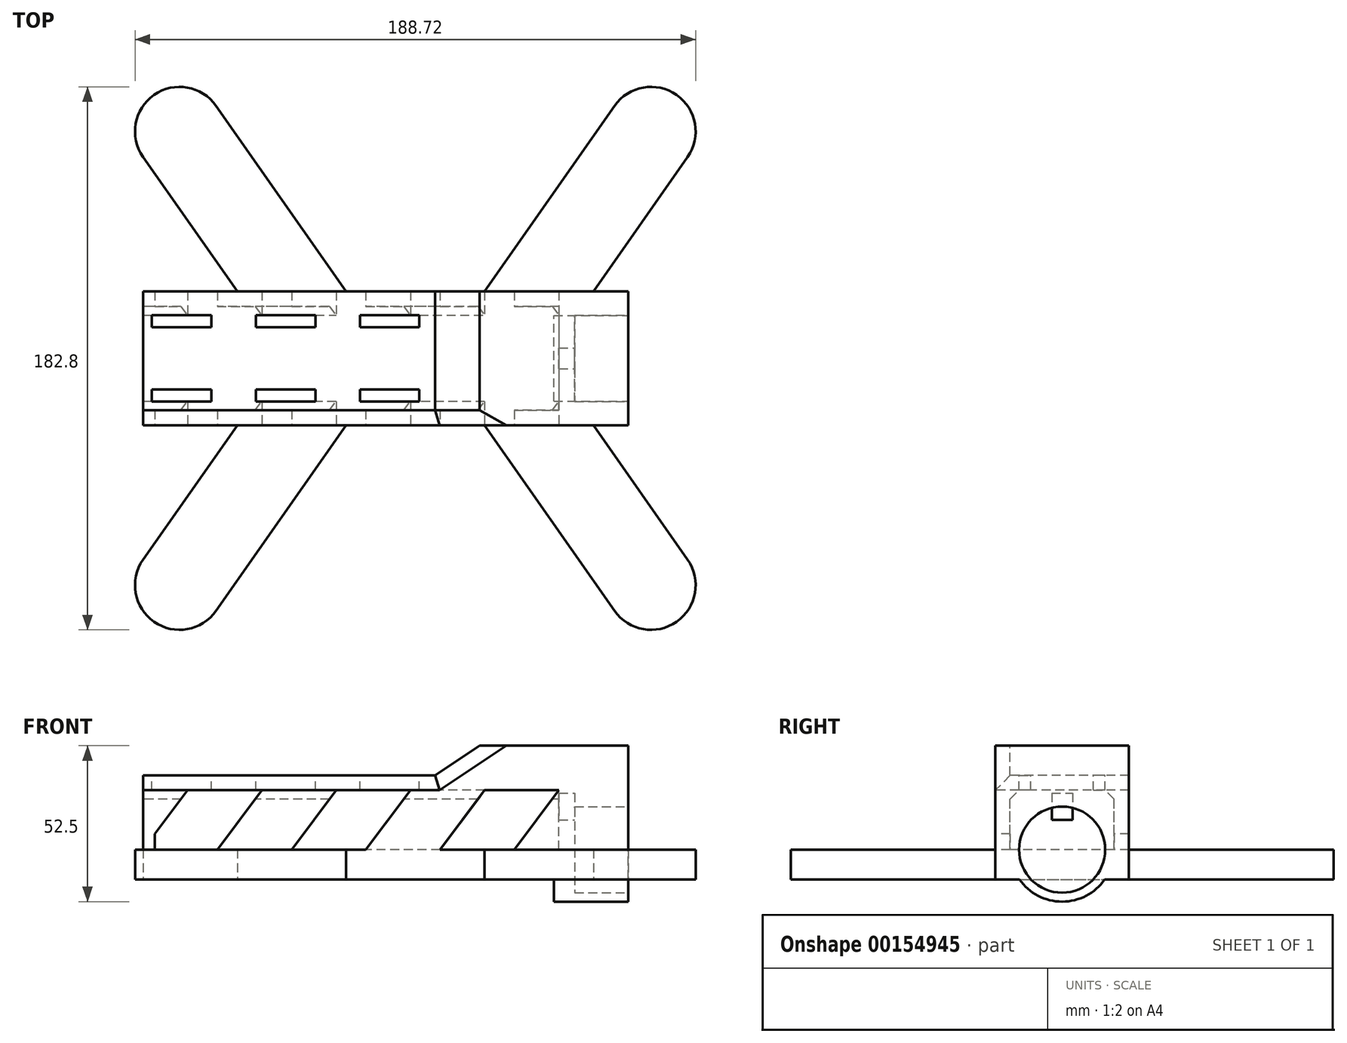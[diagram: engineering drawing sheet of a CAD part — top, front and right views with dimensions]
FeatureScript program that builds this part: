
annotation { "Feature Type Name" : "Feature", "Feature Type Description" : "" }
export const myFeature = defineFeature(function(context is Context, id is Id, definition is map)
    precondition{}
    {
        {
            var Q0;
            Q0=qCreatedBy(makeId("Top.planeOp"),FACE);
            var sketch = newSketch(context, id + "F0", { "sketchPlane" : qUnion([Q0])});
            skLineSegment(sketch, "E0.bottom", {"start": v(-91.65, 85) * mm, "end": v(91.65, 85) * mm, "construction": true});
            skLineSegment(sketch, "E0.top", {"start": v(-91.65, -85) * mm, "end": v(91.65, -85) * mm, "construction": true});
            skLineSegment(sketch, "E0.left", {"start": v(-91.65, 85) * mm, "end": v(-91.65, -85) * mm, "construction": true});
            skLineSegment(sketch, "E0.right", {"start": v(91.65, 85) * mm, "end": v(91.65, -85) * mm, "construction": true});
            skPoint(sketch, "E0.middle", {"position": v(0, 0) * mm});
            skLineSegment(sketch, "E1.bottom", {"start": v(-91.65, -22.5) * mm, "end": v(91.65, -22.5) * mm});
            skLineSegment(sketch, "E1.top", {"start": v(-91.65, 22.5) * mm, "end": v(91.65, 22.5) * mm});
            skLineSegment(sketch, "E1.left", {"start": v(-91.65, -22.5) * mm, "end": v(-91.65, 22.5) * mm});
            skLineSegment(sketch, "E1.right", {"start": v(91.65, -22.5) * mm, "end": v(91.65, 22.5) * mm});
            skLineSegment(sketch, "E2", {"start": v(-59.94, -22.5) * mm, "end": v(-91.65, -67.8) * mm});
            skLineSegment(sketch, "E3", {"start": v(-91.65, -67.8) * mm, "end": v(-67.08, -85) * mm});
            skLineSegment(sketch, "E4", {"start": v(-67.08, -85) * mm, "end": v(-23.31, -22.5) * mm});
            skCircle(sketch, "E5", {"center": v(-79.36, -76.4) * mm, "radius": 15 * mm});
            skCircle(sketch, "E6.MirrorC", {"center": v(79.36, -76.4) * mm, "radius": 15 * mm});
            skLineSegment(sketch, "E7.MirrorCS", {"start": v(59.94, -22.5) * mm, "end": v(91.65, -67.8) * mm});
            skLineSegment(sketch, "E8.MirrorCS", {"start": v(67.08, -85) * mm, "end": v(23.31, -22.5) * mm});
            skLineSegment(sketch, "E9.MirrorCS", {"start": v(59.94, 22.5) * mm, "end": v(91.65, 67.8) * mm});
            skCircle(sketch, "E10.MirrorC", {"center": v(79.36, 76.4) * mm, "radius": 15 * mm});
            skLineSegment(sketch, "E11.MirrorCS", {"start": v(67.08, 85) * mm, "end": v(23.31, 22.5) * mm});
            skCircle(sketch, "E12.MirrorC", {"center": v(-79.36, 76.4) * mm, "radius": 15 * mm});
            skLineSegment(sketch, "E13.MirrorCS", {"start": v(-67.08, 85) * mm, "end": v(-23.31, 22.5) * mm});
            skLineSegment(sketch, "E14.MirrorCS", {"start": v(-59.94, 22.5) * mm, "end": v(-91.65, 67.8) * mm});
            skSolve(sketch);
        }
        {
            var Q0;
            Q0 = qSketchRegion(id + "F0", true);
            extrude(context, id + "F1", {"entities" : qUnion([Q0]), "depth" : 45 * mm});
        }
        {
            var Q0;
            Q0=makeQuery(id+"F1.opExtrude","CAP_FACE",FACE,{"disambiguationData":[OSD([sQuery(id+"F0.wireOp",EDGE,"E1.bottom"),sQuery(id+"F0.wireOp",EDGE,"E1.top"),sQuery(id+"F0.wireOp",EDGE,"E1.left"),sQuery(id+"F0.wireOp",EDGE,"E1.right"),sQuery(id+"F0.wireOp",EDGE,"E2"),sQuery(id+"F0.wireOp",EDGE,"E4"),sQuery(id+"F0.wireOp",EDGE,"E5"),sQuery(id+"F0.wireOp",EDGE,"E6.MirrorC"),sQuery(id+"F0.wireOp",EDGE,"E7.MirrorCS"),sQuery(id+"F0.wireOp",EDGE,"E8.MirrorCS"),sQuery(id+"F0.wireOp",EDGE,"E9.MirrorCS"),sQuery(id+"F0.wireOp",EDGE,"E10.MirrorC"),sQuery(id+"F0.wireOp",EDGE,"E11.MirrorCS"),sQuery(id+"F0.wireOp",EDGE,"E12.MirrorC"),sQuery(id+"F0.wireOp",EDGE,"E13.MirrorCS"),sQuery(id+"F0.wireOp",EDGE,"E14.MirrorCS")])],"isStart":false});
            var sketch = newSketch(context, id + "F2", { "sketchPlane" : qUnion([Q0])});
            skLineSegment(sketch, "E15.bottom", {"start": v(-91.65, 22.5) * mm, "end": v(91.65, 22.5) * mm});
            skLineSegment(sketch, "E15.top", {"start": v(-91.65, -22.5) * mm, "end": v(91.65, -22.5) * mm});
            skLineSegment(sketch, "E15.left", {"start": v(-91.65, 22.5) * mm, "end": v(-91.65, -22.5) * mm});
            skLineSegment(sketch, "E15.right", {"start": v(91.65, 22.5) * mm, "end": v(91.65, -22.5) * mm});
            skPoint(sketch, "E15.middle", {"position": v(0, 0) * mm});
            skLineSegment(sketch, "E16.bottom", {"start": v(-108.28, -99.99) * mm, "end": v(108.28, -99.99) * mm});
            skLineSegment(sketch, "E16.top", {"start": v(-108.28, 99.99) * mm, "end": v(108.28, 99.99) * mm});
            skLineSegment(sketch, "E16.left", {"start": v(-108.28, -99.99) * mm, "end": v(-108.28, 99.99) * mm});
            skLineSegment(sketch, "E16.right", {"start": v(108.28, -99.99) * mm, "end": v(108.28, 99.99) * mm});
            skSolve(sketch);
        }
        {
            var Q0;
            Q0 = qSketchRegion(id + "F2", true);
            extrude(context, id + "F3", {"entities" : qUnion([Q0]), "operationType" : NewBodyOperationType.REMOVE, "oppositeDirection" : true, "depth" : 35 * mm});
        }
        {
            var Q0;
            Q0=makeQuery(id+"F1.opExtrude","SWEPT_FACE",FACE,{"disambiguationData":[OSD([sQuery(id+"F0.wireOp",EDGE,"E1.right")])]});
            var sketch = newSketch(context, id + "F4", { "sketchPlane" : qUnion([Q0])});
            skLineSegment(sketch, "E17.bottom", {"start": v(-22.5, 0) * mm, "end": v(22.5, 0) * mm});
            skLineSegment(sketch, "E17.top", {"start": v(-22.5, 45) * mm, "end": v(22.5, 45) * mm});
            skLineSegment(sketch, "E17.left", {"start": v(-22.5, 0) * mm, "end": v(-22.5, 45) * mm});
            skLineSegment(sketch, "E17.right", {"start": v(22.5, 0) * mm, "end": v(22.5, 45) * mm});
            skSolve(sketch);
        }
        {
            var Q0;
            Q0 = qSketchRegion(id + "F4", true);
            extrude(context, id + "F5", {"entities" : qUnion([Q0]), "operationType" : NewBodyOperationType.REMOVE, "oppositeDirection" : true, "depth" : 20 * mm});
        }
        {
            var Q0;
            Q0=makeQuery(id+"F5.boolean.opBoolean","COPY",FACE,{"derivedFrom":makeQuery(id+"F5.opExtrude","CAP_FACE",FACE,{"disambiguationData":[OSD([sQuery(id+"F4.wireOp",EDGE,"E17.bottom"),sQuery(id+"F4.wireOp",EDGE,"E17.top"),sQuery(id+"F4.wireOp",EDGE,"E17.left"),sQuery(id+"F4.wireOp",EDGE,"E17.right")])],"isStart":false})});
            var sketch = newSketch(context, id + "F6", { "sketchPlane" : qUnion([Q0])});
            skCircle(sketch, "E18", {"center": v(0, 10) * mm, "radius": 17.5 * mm});
            skSolve(sketch);
        }
        {
            var Q0;
            Q0 = qSketchRegion(id + "F6", true);
            extrude(context, id + "F7", {"entities" : qUnion([Q0]), "operationType" : NewBodyOperationType.ADD, "oppositeDirection" : true, "depth" : 25 * mm});
        }
        {
            var Q0;
            Q0=makeQuery(id+"F5.boolean.opBoolean","COPY",FACE,{"derivedFrom":makeQuery(id+"F5.opExtrude","CAP_FACE",FACE,{"disambiguationData":[OSD([sQuery(id+"F4.wireOp",EDGE,"E17.bottom"),sQuery(id+"F4.wireOp",EDGE,"E17.top"),sQuery(id+"F4.wireOp",EDGE,"E17.left"),sQuery(id+"F4.wireOp",EDGE,"E17.right")])],"isStart":false})});
            var sketch = newSketch(context, id + "F8", { "sketchPlane" : qUnion([Q0])});
            skCircle(sketch, "E19", {"center": v(0, 10) * mm, "radius": 14.5 * mm});
            skSolve(sketch);
        }
        {
            var Q0;
            Q0 = qSketchRegion(id + "F8", true);
            extrude(context, id + "F9", {"entities" : qUnion([Q0]), "operationType" : NewBodyOperationType.REMOVE, "oppositeDirection" : true, "depth" : 18 * mm});
        }
        {
            var Q0;
            Q0=makeQuery(id+"F9.boolean.opBoolean","COPY",FACE,{"derivedFrom":makeQuery(id+"F9.opExtrude","CAP_FACE",FACE,{"disambiguationData":[OSD([sQuery(id+"F8.wireOp",EDGE,"E19")])],"isStart":false})});
            var sketch = newSketch(context, id + "F10", { "sketchPlane" : qUnion([Q0])});
            skLineSegment(sketch, "E20.bottom", {"start": v(-3.5, 29) * mm, "end": v(3.5, 29) * mm});
            skLineSegment(sketch, "E20.top", {"start": v(-3.5, 20) * mm, "end": v(3.5, 20) * mm});
            skLineSegment(sketch, "E20.left", {"start": v(-3.5, 29) * mm, "end": v(-3.5, 20) * mm});
            skLineSegment(sketch, "E20.right", {"start": v(3.5, 29) * mm, "end": v(3.5, 20) * mm});
            skSolve(sketch);
        }
        {
            var Q0;
            Q0 = qSketchRegion(id + "F10", true);
            extrude(context, id + "F11", {"entities" : qUnion([Q0]), "operationType" : NewBodyOperationType.REMOVE, "oppositeDirection" : true, "depth" : 10 * mm});
        }
        {
            var Q0;
            Q0=makeQuery(id+"F1.opExtrude","SWEPT_FACE",FACE,{"disambiguationData":[OSD([sQuery(id+"F0.wireOp",EDGE,"E1.left")])]});
            var sketch = newSketch(context, id + "F12", { "sketchPlane" : qUnion([Q0])});
            skLineSegment(sketch, "E21.bottom", {"start": v(-17.5, 10) * mm, "end": v(17.5, 10) * mm});
            skLineSegment(sketch, "E21.top", {"start": v(-17.5, 30) * mm, "end": v(17.5, 30) * mm});
            skLineSegment(sketch, "E21.left", {"start": v(-17.5, 10) * mm, "end": v(-17.5, 30) * mm});
            skLineSegment(sketch, "E21.right", {"start": v(17.5, 10) * mm, "end": v(17.5, 30) * mm});
            skPoint(sketch, "E21.middle", {"position": v(0, 20) * mm});
            skSolve(sketch);
        }
        {
            var Q0;
            Q0 = qSketchRegion(id + "F12", true);
            var Q1;
            Q1=makeQuery(id+"F9.boolean.opBoolean","COPY",FACE,{"derivedFrom":makeQuery(id+"F9.opExtrude","CAP_FACE",FACE,{"disambiguationData":[OSD([sQuery(id+"F8.wireOp",EDGE,"E19")])],"isStart":false})});
            extrude(context, id + "F13", {"entities" : qUnion([Q0]), "operationType" : NewBodyOperationType.REMOVE, "oppositeDirection" : true, "endBoundEntityFace" : qUnion([Q1]), "depth" : 140 * mm});
        }
        {
            var Q0;
            {var subQ0=sQuery(id+"F0.wireOp",EDGE,"E1.top");Q0=makeQuery(id+"F3.boolean.opBoolean","MERGE",FACE,{"derivedFrom":[makeQuery(id+"F1.opExtrude","SWEPT_FACE",FACE,{"disambiguationData":[OSD([subQ0]),TDD([makeQuery(id+"F0.imprint","IMPRINT",EDGE,{"disambiguationData":[TD([[makeQuery(id+"F0.imprint","INTERSECT",VERTEX,{"derivedFrom":[subQ0,sQuery(id+"F0.wireOp",EDGE,"E1.left")]}),-1.0]])],"derivedFrom":subQ0})])]}),makeQuery(id+"F1.opExtrude","SWEPT_FACE",FACE,{"disambiguationData":[OSD([subQ0]),TDD([makeQuery(id+"F0.imprint","IMPRINT",EDGE,{"disambiguationData":[TD([[makeQuery(id+"F0.imprint","INTERSECT",VERTEX,{"derivedFrom":[subQ0,sQuery(id+"F0.wireOp",EDGE,"E11.MirrorCS")]}),1.0]])],"derivedFrom":subQ0})])]}),makeQuery(id+"F1.opExtrude","SWEPT_FACE",FACE,{"disambiguationData":[OSD([subQ0]),TDD([makeQuery(id+"F0.imprint","IMPRINT",EDGE,{"disambiguationData":[TD([[makeQuery(id+"F0.imprint","INTERSECT",VERTEX,{"derivedFrom":[subQ0,sQuery(id+"F0.wireOp",EDGE,"E1.right")]}),1.0]])],"derivedFrom":subQ0})])]}),makeQuery(id+"F3.opExtrude","SWEPT_FACE",FACE,{"disambiguationData":[OSD([sQuery(id+"F2.wireOp",EDGE,"E15.bottom")])]})]});}
            var sketch = newSketch(context, id + "F14", { "sketchPlane" : qUnion([Q0])});
            skLineSegment(sketch, "E22", {"start": v(-21.65, 45) * mm, "end": v(-6.65, 35) * mm});
            skLineSegment(sketch, "E23", {"start": v(-6.65, 35) * mm, "end": v(91.65, 35) * mm});
            skLineSegment(sketch, "E24", {"start": v(91.65, 35) * mm, "end": v(106.87, 35) * mm});
            skLineSegment(sketch, "E25", {"start": v(106.87, 35) * mm, "end": v(106.87, 69.96) * mm});
            skLineSegment(sketch, "E26", {"start": v(106.87, 69.96) * mm, "end": v(-21.65, 69.96) * mm});
            skLineSegment(sketch, "E27", {"start": v(-21.65, 69.96) * mm, "end": v(-21.65, 45) * mm});
            skSolve(sketch);
        }
        {
            var Q0;
            Q0 = qSketchRegion(id + "F14", true);
            extrude(context, id + "F15", {"entities" : qUnion([Q0]), "operationType" : NewBodyOperationType.REMOVE, "endBound" : BoundingType.THROUGH_ALL, "oppositeDirection" : true, "depth" : 25 * mm});
        }
        {
            var Q0;
            {var subQ0=sQuery(id+"F0.wireOp",EDGE,"E1.top");Q0=makeQuery(id+"F3.boolean.opBoolean","MERGE",EDGE,{"derivedFrom":[makeQuery(id+"F1.opExtrude","CAP_EDGE",EDGE,{"disambiguationData":[OSD([subQ0]),TDD([makeQuery(id+"F0.imprint","IMPRINT",EDGE,{"disambiguationData":[TD([[makeQuery(id+"F0.imprint","INTERSECT",VERTEX,{"derivedFrom":[subQ0,sQuery(id+"F0.wireOp",EDGE,"E1.left")]}),-1.0]])],"derivedFrom":subQ0})])],"isStart":false}),makeQuery(id+"F1.opExtrude","CAP_EDGE",EDGE,{"disambiguationData":[OSD([subQ0]),TDD([makeQuery(id+"F0.imprint","IMPRINT",EDGE,{"disambiguationData":[TD([[makeQuery(id+"F0.imprint","INTERSECT",VERTEX,{"derivedFrom":[subQ0,sQuery(id+"F0.wireOp",EDGE,"E11.MirrorCS")]}),1.0]])],"derivedFrom":subQ0})])],"isStart":false}),makeQuery(id+"F1.opExtrude","CAP_EDGE",EDGE,{"disambiguationData":[OSD([subQ0]),TDD([makeQuery(id+"F0.imprint","IMPRINT",EDGE,{"disambiguationData":[TD([[makeQuery(id+"F0.imprint","INTERSECT",VERTEX,{"derivedFrom":[subQ0,sQuery(id+"F0.wireOp",EDGE,"E1.right")]}),1.0]])],"derivedFrom":subQ0})])],"isStart":false}),makeQuery(id+"F3.opExtrude","CAP_EDGE",EDGE,{"disambiguationData":[OSD([sQuery(id+"F2.wireOp",EDGE,"E15.bottom")])],"isStart":true})]});}
            var Q1;
            {var subQ0=sQuery(id+"F0.wireOp",EDGE,"E1.bottom");Q1=makeQuery(id+"F3.boolean.opBoolean","MERGE",EDGE,{"derivedFrom":[makeQuery(id+"F1.opExtrude","CAP_EDGE",EDGE,{"disambiguationData":[OSD([subQ0]),TDD([makeQuery(id+"F0.imprint","IMPRINT",EDGE,{"disambiguationData":[TD([[makeQuery(id+"F0.imprint","INTERSECT",VERTEX,{"derivedFrom":[subQ0,sQuery(id+"F0.wireOp",EDGE,"E1.left")]}),-1.0]])],"derivedFrom":subQ0})])],"isStart":false}),makeQuery(id+"F1.opExtrude","CAP_EDGE",EDGE,{"disambiguationData":[OSD([subQ0]),TDD([makeQuery(id+"F0.imprint","IMPRINT",EDGE,{"disambiguationData":[TD([[makeQuery(id+"F0.imprint","INTERSECT",VERTEX,{"derivedFrom":[subQ0,sQuery(id+"F0.wireOp",EDGE,"E4")]}),-1.0]])],"derivedFrom":subQ0})])],"isStart":false}),makeQuery(id+"F1.opExtrude","CAP_EDGE",EDGE,{"disambiguationData":[OSD([subQ0]),TDD([makeQuery(id+"F0.imprint","IMPRINT",EDGE,{"disambiguationData":[TD([[makeQuery(id+"F0.imprint","INTERSECT",VERTEX,{"derivedFrom":[subQ0,sQuery(id+"F0.wireOp",EDGE,"E1.right")]}),1.0]])],"derivedFrom":subQ0})])],"isStart":false}),makeQuery(id+"F3.opExtrude","CAP_EDGE",EDGE,{"disambiguationData":[OSD([sQuery(id+"F2.wireOp",EDGE,"E15.top")])],"isStart":true})]});}
            var Q2;
            {var subQ0=sQuery(id+"F0.wireOp",EDGE,"E1.bottom");Q2=makeQuery(id+"F15.boolean.opBoolean","INTERSECT",EDGE,{"derivedFrom":[makeQuery(id+"F3.boolean.opBoolean","MERGE",FACE,{"derivedFrom":[makeQuery(id+"F1.opExtrude","SWEPT_FACE",FACE,{"disambiguationData":[OSD([subQ0]),TDD([makeQuery(id+"F0.imprint","IMPRINT",EDGE,{"disambiguationData":[TD([[makeQuery(id+"F0.imprint","INTERSECT",VERTEX,{"derivedFrom":[subQ0,sQuery(id+"F0.wireOp",EDGE,"E1.left")]}),-1.0]])],"derivedFrom":subQ0})])]}),makeQuery(id+"F1.opExtrude","SWEPT_FACE",FACE,{"disambiguationData":[OSD([subQ0]),TDD([makeQuery(id+"F0.imprint","IMPRINT",EDGE,{"disambiguationData":[TD([[makeQuery(id+"F0.imprint","INTERSECT",VERTEX,{"derivedFrom":[subQ0,sQuery(id+"F0.wireOp",EDGE,"E4")]}),-1.0]])],"derivedFrom":subQ0})])]}),makeQuery(id+"F1.opExtrude","SWEPT_FACE",FACE,{"disambiguationData":[OSD([subQ0]),TDD([makeQuery(id+"F0.imprint","IMPRINT",EDGE,{"disambiguationData":[TD([[makeQuery(id+"F0.imprint","INTERSECT",VERTEX,{"derivedFrom":[subQ0,sQuery(id+"F0.wireOp",EDGE,"E1.right")]}),1.0]])],"derivedFrom":subQ0})])]}),makeQuery(id+"F3.opExtrude","SWEPT_FACE",FACE,{"disambiguationData":[OSD([sQuery(id+"F2.wireOp",EDGE,"E15.top")])]})]}),makeQuery(id+"F15.opExtrude","SWEPT_FACE",FACE,{"disambiguationData":[OSD([sQuery(id+"F14.wireOp",EDGE,"E22")])]})]});}
            var Q3;
            Q3=makeQuery(id+"F15.boolean.opBoolean","COPY",EDGE,{"derivedFrom":makeQuery(id+"F15.opExtrude","CAP_EDGE",EDGE,{"disambiguationData":[OSD([sQuery(id+"F14.wireOp",EDGE,"E22")])],"isStart":true})});
            var Q4;
            Q4=makeQuery(id+"F15.boolean.opBoolean","COPY",EDGE,{"derivedFrom":makeQuery(id+"F15.opExtrude","CAP_EDGE",EDGE,{"disambiguationData":[OSD([sQuery(id+"F14.wireOp",EDGE,"E23"),sQuery(id+"F14.wireOp",EDGE,"E24")])],"isStart":true})});
            var Q5;
            {var subQ0=sQuery(id+"F0.wireOp",EDGE,"E1.bottom");Q5=makeQuery(id+"F15.boolean.opBoolean","INTERSECT",EDGE,{"derivedFrom":[makeQuery(id+"F3.boolean.opBoolean","MERGE",FACE,{"derivedFrom":[makeQuery(id+"F1.opExtrude","SWEPT_FACE",FACE,{"disambiguationData":[OSD([subQ0]),TDD([makeQuery(id+"F0.imprint","IMPRINT",EDGE,{"disambiguationData":[TD([[makeQuery(id+"F0.imprint","INTERSECT",VERTEX,{"derivedFrom":[subQ0,sQuery(id+"F0.wireOp",EDGE,"E1.left")]}),-1.0]])],"derivedFrom":subQ0})])]}),makeQuery(id+"F1.opExtrude","SWEPT_FACE",FACE,{"disambiguationData":[OSD([subQ0]),TDD([makeQuery(id+"F0.imprint","IMPRINT",EDGE,{"disambiguationData":[TD([[makeQuery(id+"F0.imprint","INTERSECT",VERTEX,{"derivedFrom":[subQ0,sQuery(id+"F0.wireOp",EDGE,"E4")]}),-1.0]])],"derivedFrom":subQ0})])]}),makeQuery(id+"F1.opExtrude","SWEPT_FACE",FACE,{"disambiguationData":[OSD([subQ0]),TDD([makeQuery(id+"F0.imprint","IMPRINT",EDGE,{"disambiguationData":[TD([[makeQuery(id+"F0.imprint","INTERSECT",VERTEX,{"derivedFrom":[subQ0,sQuery(id+"F0.wireOp",EDGE,"E1.right")]}),1.0]])],"derivedFrom":subQ0})])]}),makeQuery(id+"F3.opExtrude","SWEPT_FACE",FACE,{"disambiguationData":[OSD([sQuery(id+"F2.wireOp",EDGE,"E15.top")])]})]}),makeQuery(id+"F15.opExtrude","SWEPT_FACE",FACE,{"disambiguationData":[OSD([sQuery(id+"F14.wireOp",EDGE,"E23"),sQuery(id+"F14.wireOp",EDGE,"E24")])]})]});}
            chamfer(context, id + "F16", {"entities" : qUnion([Q0, Q1, Q2, Q3, Q4, Q5]), "width" : 5 * mm, "tangentPropagation" : true});
        }
        {
            var Q0;
            Q0=makeQuery(id+"F13.boolean.opBoolean","COPY",EDGE,{"derivedFrom":makeQuery(id+"F13.opExtrude","SWEPT_EDGE",EDGE,{"disambiguationData":[OSD([sQuery(id+"F12.wireOp",EDGE,"E21.top"),sQuery(id+"F12.wireOp",EDGE,"E21.left")])]})});
            var Q1;
            Q1=makeQuery(id+"F13.boolean.opBoolean","COPY",EDGE,{"derivedFrom":makeQuery(id+"F13.opExtrude","SWEPT_EDGE",EDGE,{"disambiguationData":[OSD([sQuery(id+"F12.wireOp",EDGE,"E21.top"),sQuery(id+"F12.wireOp",EDGE,"E21.right")])]})});
            chamfer(context, id + "F17", {"entities" : qUnion([Q0, Q1]), "width" : 3 * mm, "tangentPropagation" : true});
        }
        {
            var Q0;
            Q0=makeQuery(id+"F15.boolean.opBoolean","COPY",FACE,{"derivedFrom":makeQuery(id+"F15.opExtrude","SWEPT_FACE",FACE,{"disambiguationData":[OSD([sQuery(id+"F14.wireOp",EDGE,"E23"),sQuery(id+"F14.wireOp",EDGE,"E24")])]})});
            var sketch = newSketch(context, id + "F18", { "sketchPlane" : qUnion([Q0])});
            skLineSegment(sketch, "E28.bottom", {"start": v(-88.65, 14.5) * mm, "end": v(-68.65, 14.5) * mm});
            skLineSegment(sketch, "E28.top", {"start": v(-88.65, 10.5) * mm, "end": v(-68.65, 10.5) * mm});
            skLineSegment(sketch, "E28.left", {"start": v(-88.65, 14.5) * mm, "end": v(-88.65, 10.5) * mm});
            skLineSegment(sketch, "E28.right", {"start": v(-68.65, 14.5) * mm, "end": v(-68.65, 10.5) * mm});
            skLineSegment(sketch, "E29.1.0.0", {"start": v(-53.65, 10.5) * mm, "end": v(-33.65, 10.5) * mm});
            skLineSegment(sketch, "E29.1.0.1", {"start": v(-33.65, 14.5) * mm, "end": v(-33.65, 10.5) * mm});
            skLineSegment(sketch, "E29.1.0.2", {"start": v(-53.65, 14.5) * mm, "end": v(-33.65, 14.5) * mm});
            skLineSegment(sketch, "E29.1.0.3", {"start": v(-53.65, 14.5) * mm, "end": v(-53.65, 10.5) * mm});
            skLineSegment(sketch, "E29.2.0.0", {"start": v(-18.65, 10.5) * mm, "end": v(1.35, 10.5) * mm});
            skLineSegment(sketch, "E29.2.0.1", {"start": v(1.35, 14.5) * mm, "end": v(1.35, 10.5) * mm});
            skLineSegment(sketch, "E29.2.0.2", {"start": v(-18.65, 14.5) * mm, "end": v(1.35, 14.5) * mm});
            skLineSegment(sketch, "E29.2.0.3", {"start": v(-18.65, 14.5) * mm, "end": v(-18.65, 10.5) * mm});
            skLineSegment(sketch, "E29.direction1", {"start": v(-88.65, 10.5) * mm, "end": v(-53.65, 10.5) * mm, "construction": true});
            skLineSegment(sketch, "E30.MirrorCS", {"start": v(-88.65, -10.5) * mm, "end": v(-68.65, -10.5) * mm});
            skLineSegment(sketch, "E31.MirrorCS", {"start": v(-18.65, -14.5) * mm, "end": v(-18.65, -10.5) * mm});
            skLineSegment(sketch, "E32.MirrorCS", {"start": v(-18.65, -14.5) * mm, "end": v(1.35, -14.5) * mm});
            skLineSegment(sketch, "E33.MirrorCS", {"start": v(1.35, -14.5) * mm, "end": v(1.35, -10.5) * mm});
            skLineSegment(sketch, "E34.MirrorCS", {"start": v(-18.65, -10.5) * mm, "end": v(1.35, -10.5) * mm});
            skLineSegment(sketch, "E35.MirrorCS", {"start": v(-53.65, -14.5) * mm, "end": v(-53.65, -10.5) * mm});
            skLineSegment(sketch, "E36.MirrorCS", {"start": v(-53.65, -14.5) * mm, "end": v(-33.65, -14.5) * mm});
            skLineSegment(sketch, "E37.MirrorCS", {"start": v(-33.65, -14.5) * mm, "end": v(-33.65, -10.5) * mm});
            skLineSegment(sketch, "E38.MirrorCS", {"start": v(-53.65, -10.5) * mm, "end": v(-33.65, -10.5) * mm});
            skLineSegment(sketch, "E39.MirrorCS", {"start": v(-68.65, -14.5) * mm, "end": v(-68.65, -10.5) * mm});
            skLineSegment(sketch, "E40.MirrorCS", {"start": v(-88.65, -14.5) * mm, "end": v(-68.65, -14.5) * mm});
            skLineSegment(sketch, "E41.MirrorCS", {"start": v(-88.65, -14.5) * mm, "end": v(-88.65, -10.5) * mm});
            skSolve(sketch);
        }
        {
            var Q0;
            Q0 = qSketchRegion(id + "F18", true);
            extrude(context, id + "F19", {"entities" : qUnion([Q0]), "operationType" : NewBodyOperationType.REMOVE, "oppositeDirection" : true, "depth" : 10 * mm});
        }
        {
            var Q0;
            {var subQ0=sQuery(id+"F0.wireOp",EDGE,"E1.bottom");Q0=makeQuery(id+"F3.boolean.opBoolean","MERGE",FACE,{"derivedFrom":[makeQuery(id+"F1.opExtrude","SWEPT_FACE",FACE,{"disambiguationData":[OSD([subQ0]),TDD([makeQuery(id+"F0.imprint","IMPRINT",EDGE,{"disambiguationData":[TD([[makeQuery(id+"F0.imprint","INTERSECT",VERTEX,{"derivedFrom":[subQ0,sQuery(id+"F0.wireOp",EDGE,"E1.left")]}),-1.0]])],"derivedFrom":subQ0})])]}),makeQuery(id+"F1.opExtrude","SWEPT_FACE",FACE,{"disambiguationData":[OSD([subQ0]),TDD([makeQuery(id+"F0.imprint","IMPRINT",EDGE,{"disambiguationData":[TD([[makeQuery(id+"F0.imprint","INTERSECT",VERTEX,{"derivedFrom":[subQ0,sQuery(id+"F0.wireOp",EDGE,"E4")]}),-1.0]])],"derivedFrom":subQ0})])]}),makeQuery(id+"F1.opExtrude","SWEPT_FACE",FACE,{"disambiguationData":[OSD([subQ0]),TDD([makeQuery(id+"F0.imprint","IMPRINT",EDGE,{"disambiguationData":[TD([[makeQuery(id+"F0.imprint","INTERSECT",VERTEX,{"derivedFrom":[subQ0,sQuery(id+"F0.wireOp",EDGE,"E1.right")]}),1.0]])],"derivedFrom":subQ0})])]}),makeQuery(id+"F3.opExtrude","SWEPT_FACE",FACE,{"disambiguationData":[OSD([sQuery(id+"F2.wireOp",EDGE,"E15.top")])]})]});}
            var sketch = newSketch(context, id + "F20", { "sketchPlane" : qUnion([Q0])});
            skLineSegment(sketch, "E42.bottom", {"start": v(-91.65, 30) * mm, "end": v(48.35, 30) * mm});
            skLineSegment(sketch, "E42.top", {"start": v(-91.65, 10) * mm, "end": v(48.35, 10) * mm});
            skLineSegment(sketch, "E42.left", {"start": v(-91.65, 30) * mm, "end": v(-91.65, 10) * mm});
            skLineSegment(sketch, "E42.right", {"start": v(48.35, 30) * mm, "end": v(48.35, 10) * mm});
            skLineSegment(sketch, "E43", {"start": v(-91.65, 10) * mm, "end": v(-76.65, 30) * mm});
            skLineSegment(sketch, "E44.1.0.0", {"start": v(-66.65, 10) * mm, "end": v(-51.65, 30) * mm});
            skLineSegment(sketch, "E44.2.0.0", {"start": v(-41.65, 10) * mm, "end": v(-26.65, 30) * mm});
            skLineSegment(sketch, "E44.3.0.0", {"start": v(-16.65, 10) * mm, "end": v(-1.65, 30) * mm});
            skLineSegment(sketch, "E44.4.0.0", {"start": v(8.35, 10) * mm, "end": v(23.35, 30) * mm});
            skLineSegment(sketch, "E44.5.0.0", {"start": v(33.35, 10) * mm, "end": v(48.35, 30) * mm});
            skLineSegment(sketch, "E44.direction1", {"start": v(-91.65, 10) * mm, "end": v(-66.65, 10) * mm, "construction": true});
            skLineSegment(sketch, "E45.bottom", {"start": v(-91.65, 30) * mm, "end": v(-87.65, 30) * mm});
            skLineSegment(sketch, "E45.top", {"start": v(-91.65, 10) * mm, "end": v(-87.65, 10) * mm});
            skLineSegment(sketch, "E45.right", {"start": v(-87.65, 30) * mm, "end": v(-87.65, 10) * mm});
            skSolve(sketch);
        }
        {
            var Q0;
            {var subQ0=sQuery(id+"F20.wireOp",EDGE,"E44.1.0.0");Q0=makeQuery(id+"F20.imprint","IMPRINT",FACE,{"disambiguationData":[TD([[makeQuery(id+"F20.imprint","IMPRINT",EDGE,{"derivedFrom":subQ0}),1.0]])]});}
            var Q1;
            {var subQ0=sQuery(id+"F20.wireOp",EDGE,"E44.2.0.0");Q1=makeQuery(id+"F20.imprint","IMPRINT",FACE,{"disambiguationData":[TD([[makeQuery(id+"F20.imprint","IMPRINT",EDGE,{"derivedFrom":subQ0}),-1.0]])]});}
            var Q2;
            {var subQ0=sQuery(id+"F20.wireOp",EDGE,"E44.4.0.0");Q2=makeQuery(id+"F20.imprint","IMPRINT",FACE,{"disambiguationData":[TD([[makeQuery(id+"F20.imprint","IMPRINT",EDGE,{"derivedFrom":subQ0}),-1.0]])]});}
            extrude(context, id + "F21", {"entities" : qUnion([Q0, Q1, Q2]), "operationType" : NewBodyOperationType.REMOVE, "endBound" : BoundingType.THROUGH_ALL, "oppositeDirection" : true, "depth" : 25 * mm});
        }
    });
